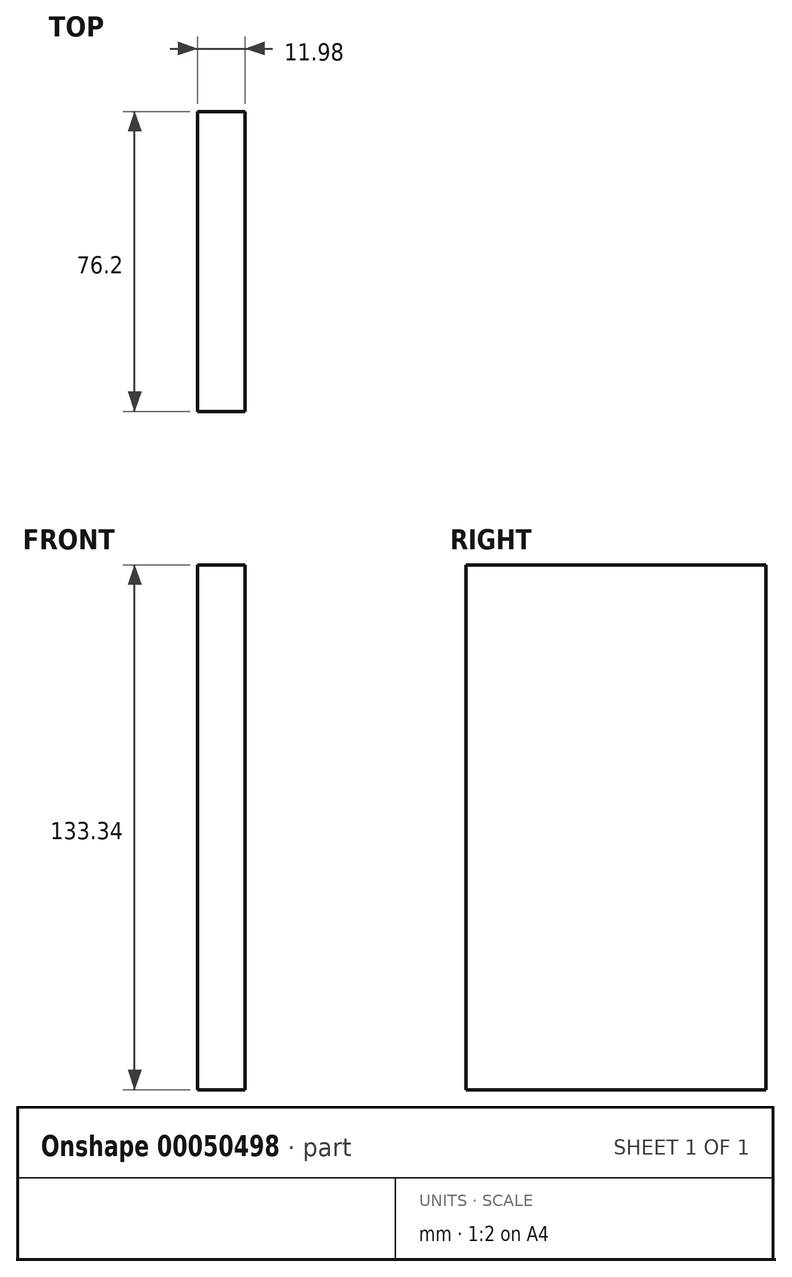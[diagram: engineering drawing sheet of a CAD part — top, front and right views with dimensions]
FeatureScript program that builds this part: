
annotation { "Feature Type Name" : "Feature", "Feature Type Description" : "" }
export const myFeature = defineFeature(function(context is Context, id is Id, definition is map)
    precondition{}
    {
        {
            var Q0;
            Q0=qCreatedBy(makeId("Right.planeOp"),FACE);
            var sketch = newSketch(context, id + "F0", { "sketchPlane" : qUnion([Q0])});
            skLineSegment(sketch, "E0.rect.bottom", {"start": v(38.1, 66.68) * mm, "end": v(-38.1, 66.68) * mm});
            skLineSegment(sketch, "E0.rect.top", {"start": v(38.1, -66.68) * mm, "end": v(-38.1, -66.68) * mm});
            skLineSegment(sketch, "E0.rect.left", {"start": v(38.1, 66.68) * mm, "end": v(38.1, -66.68) * mm});
            skLineSegment(sketch, "E0.rect.right", {"start": v(-38.1, 66.68) * mm, "end": v(-38.1, -66.68) * mm});
            skPoint(sketch, "E0.rect.middle", {"position": v(0, 0) * mm});
            skSolve(sketch);
        }
        {
            var Q0;
            Q0 = qSketchRegion(id + "F0", true);
            extrude(context, id + "F1", {"entities" : qUnion([Q0]), "endBound" : BoundingType.SYMMETRIC, "depth" : 12 * mm});
        }
    });
